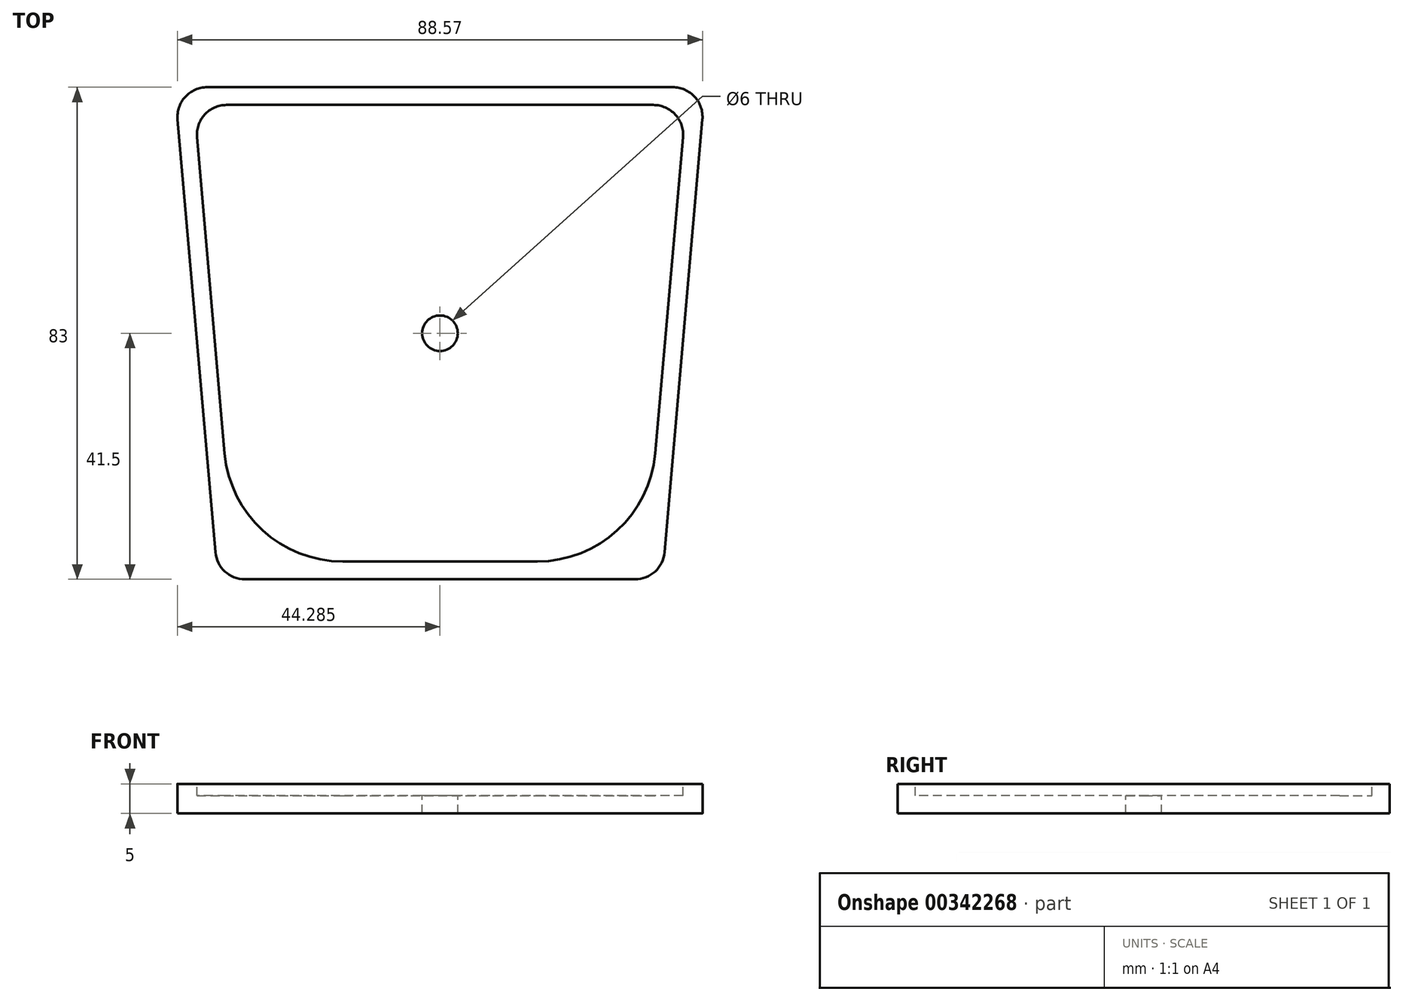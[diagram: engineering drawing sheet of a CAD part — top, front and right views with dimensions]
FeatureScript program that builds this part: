
annotation { "Feature Type Name" : "Feature", "Feature Type Description" : "" }
export const myFeature = defineFeature(function(context is Context, id is Id, definition is map)
    precondition{}
    {
        {
            var Q0;
            Q0=qCreatedBy(makeId("Top.planeOp"),FACE);
            var sketch = newSketch(context, id + "F0", { "sketchPlane" : qUnion([Q0])});
            skLineSegment(sketch, "E0.bottom", {"start": v(-48.45, 0) * mm, "end": v(41.55, 0) * mm});
            skLineSegment(sketch, "E0.top", {"start": v(-40.93, -86) * mm, "end": v(34.02, -86) * mm});
            skLineSegment(sketch, "E0.left", {"start": v(-48.45, 0) * mm, "end": v(-40.93, -86) * mm});
            skLineSegment(sketch, "E0.right", {"start": v(41.55, 0) * mm, "end": v(34.02, -86) * mm});
            skSolve(sketch);
        }
        {
            var Q0;
            Q0=makeQuery(id+"F0.imprint","IMPRINT",FACE,{"disambiguationData":[TD([[makeQuery(id+"F0.imprint","IMPRINT",EDGE,{"derivedFrom":sQuery(id+"F0.wireOp",EDGE,"E0.bottom")}),-1.0]])]});
            extrude(context, id + "F1", {"entities" : qUnion([Q0]), "depth" : 10 * mm});
        }
        {
            var Q0;
            Q0=makeQuery(id+"F1.opExtrude","SWEPT_FACE",FACE,{"disambiguationData":[OSD([sQuery(id+"F0.wireOp",EDGE,"E0.bottom")])]});
            var sketch = newSketch(context, id + "F2", { "sketchPlane" : qUnion([Q0])});
            skLineSegment(sketch, "E1.bottom", {"start": v(-41.55, -40) * mm, "end": v(48.45, -40) * mm});
            skLineSegment(sketch, "E1.top", {"start": v(-41.55, 50) * mm, "end": v(48.45, 50) * mm});
            skLineSegment(sketch, "E1.left", {"start": v(-41.55, -40) * mm, "end": v(-41.55, 50) * mm});
            skLineSegment(sketch, "E1.right", {"start": v(48.45, -40) * mm, "end": v(48.45, 50) * mm});
            skSolve(sketch);
        }
        {
            var Q0;
            {var subQ0=sQuery(id+"F2.wireOp",EDGE,"E1.top");Q0=makeQuery(id+"F2.imprint","IMPRINT",FACE,{"disambiguationData":[TD([[makeQuery(id+"F2.imprint","IMPRINT",EDGE,{"derivedFrom":subQ0}),-1.0]])]});}
            var Q1;
            {var subQ1=sQuery(id+"F0.wireOp",EDGE,"E0.bottom");var subQ2=makeQuery(id+"F1.opExtrude","CAP_EDGE",EDGE,{"disambiguationData":[OSD([subQ1])],"isStart":true});Q1=makeQuery(id+"F2.imprint","IMPRINT",FACE,{"disambiguationData":[TD([[makeQuery(id+"F2.imprint","IMPRINT",EDGE,{"derivedFrom":subQ2}),-1.0]])]});}
            var Q2;
            {var subQ0=sQuery(id+"F2.wireOp",EDGE,"E1.bottom");Q2=makeQuery(id+"F2.imprint","IMPRINT",FACE,{"disambiguationData":[TD([[makeQuery(id+"F2.imprint","IMPRINT",EDGE,{"derivedFrom":subQ0}),1.0]])]});}
            extrude(context, id + "F3", {"entities" : qUnion([Q0, Q1, Q2]), "operationType" : NewBodyOperationType.ADD, "depth" : 10 * mm});
        }
        {
            var Q0;
            Q0=makeQuery(id+"F1.opExtrude","SWEPT_EDGE",EDGE,{"disambiguationData":[OSD([sQuery(id+"F0.wireOp",EDGE,"E0.top"),sQuery(id+"F0.wireOp",EDGE,"E0.left")])]});
            var Q1;
            Q1=makeQuery(id+"F1.opExtrude","SWEPT_EDGE",EDGE,{"disambiguationData":[OSD([sQuery(id+"F0.wireOp",EDGE,"E0.top"),sQuery(id+"F0.wireOp",EDGE,"E0.right")])]});
            fillet(context, id + "F4", {"entities" : qUnion([Q0, Q1]), "radius" : 5 * mm, "tangentPropagation" : true, "allowEdgeOverflow" : false});
        }
        {
            var Q0;
            {var subQ0=sQuery(id+"F2.wireOp",EDGE,"E1.top");var subQ3=sQuery(id+"F2.wireOp",EDGE,"E1.left");var subQ4=sQuery(id+"F2.wireOp",EDGE,"E1.right");Q0=makeQuery(id+"F3.boolean.opBoolean","SPLIT",FACE,{"disambiguationData":[TD([makeQuery(id+"F3.opExtrude","SWEPT_FACE",FACE,{"disambiguationData":[OSD([subQ0])]})])],"derivedFrom":makeQuery(id+"F3.opExtrude","CAP_FACE",FACE,{"disambiguationData":[OSD([sQuery(id+"F2.wireOp",EDGE,"E1.bottom"),subQ0,subQ3,subQ4])],"isStart":true})});}
            var sketch = newSketch(context, id + "F5", { "sketchPlane" : qUnion([Q0])});
            skCircle(sketch, "E2", {"center": v(-28.45, 40) * mm, "radius": 4 * mm});
            skCircle(sketch, "E3", {"center": v(21.55, 40) * mm, "radius": 4 * mm});
            skSolve(sketch);
        }
        {
            var Q0;
            Q0 = qSketchRegion(id + "F5", true);
            extrude(context, id + "F6", {"entities" : qUnion([Q0]), "operationType" : NewBodyOperationType.REMOVE, "oppositeDirection" : true, "depth" : 25 * mm});
        }
        {
            var Q0;
            Q0=makeQuery(id+"F3.opExtrude","SWEPT_EDGE",EDGE,{"disambiguationData":[OSD([sQuery(id+"F2.wireOp",EDGE,"E1.top"),sQuery(id+"F2.wireOp",EDGE,"E1.right")])]});
            var Q1;
            Q1=makeQuery(id+"F3.opExtrude","SWEPT_EDGE",EDGE,{"disambiguationData":[OSD([sQuery(id+"F2.wireOp",EDGE,"E1.top"),sQuery(id+"F2.wireOp",EDGE,"E1.left")])]});
            var Q2;
            Q2=makeQuery(id+"F3.opExtrude","SWEPT_EDGE",EDGE,{"disambiguationData":[OSD([sQuery(id+"F2.wireOp",EDGE,"E1.bottom"),sQuery(id+"F2.wireOp",EDGE,"E1.left")])]});
            var Q3;
            Q3=makeQuery(id+"F3.opExtrude","SWEPT_EDGE",EDGE,{"disambiguationData":[OSD([sQuery(id+"F2.wireOp",EDGE,"E1.bottom"),sQuery(id+"F2.wireOp",EDGE,"E1.right")])]});
            fillet(context, id + "F7", {"entities" : qUnion([Q0, Q1, Q2, Q3]), "radius" : 3 * mm, "tangentPropagation" : true, "allowEdgeOverflow" : false});
        }
        {
            var Q0;
            Q0=makeQuery(id+"F1.opExtrude","CAP_EDGE",EDGE,{"disambiguationData":[OSD([sQuery(id+"F0.wireOp",EDGE,"E0.bottom")])],"isStart":false});
            fillet(context, id + "F8", {"entities" : qUnion([Q0]), "radius" : 3 * mm, "tangentPropagation" : true, "allowEdgeOverflow" : false});
        }
        {
            var Q0;
            Q0=makeQuery(id+"F1.opExtrude","CAP_FACE",FACE,{"disambiguationData":[OSD([sQuery(id+"F0.wireOp",EDGE,"E0.bottom"),sQuery(id+"F0.wireOp",EDGE,"E0.top"),sQuery(id+"F0.wireOp",EDGE,"E0.left"),sQuery(id+"F0.wireOp",EDGE,"E0.right")])],"isStart":false});
            var sketch = newSketch(context, id + "F9", { "sketchPlane" : qUnion([Q0])});
            skLineSegment(sketch, "E4.0", {"start": v(32.55, -6) * mm, "end": v(-39.46, -6) * mm});
            skLineSegment(sketch, "E4.1", {"start": v(37.53, -11.44) * mm, "end": v(32.87, -64.74) * mm});
            skLineSegment(sketch, "E4.2", {"start": v(-19.86, -83) * mm, "end": v(12.95, -83) * mm});
            skLineSegment(sketch, "E4.3", {"start": v(-44.44, -11.44) * mm, "end": v(-39.78, -64.74) * mm});
            skPoint(sketch, "E5.visualSharp", {"position": v(-44.92, -6) * mm});
            skArc(sketch, "E5.filletArc", {"start": v(-39.46, -6) * mm, "mid": v(-43.15, -7.62) * mm, "end": v(-44.44, -11.44) * mm});
            skPoint(sketch, "E6.visualSharp", {"position": v(-38.18, -83) * mm});
            skArc(sketch, "E6.filletArc", {"start": v(-39.78, -64.74) * mm, "mid": v(-33.37, -77.75) * mm, "end": v(-19.86, -83) * mm});
            skPoint(sketch, "E7.visualSharp", {"position": v(31.27, -83) * mm});
            skArc(sketch, "E7.filletArc", {"start": v(12.95, -83) * mm, "mid": v(26.46, -77.75) * mm, "end": v(32.87, -64.74) * mm});
            skPoint(sketch, "E8.visualSharp", {"position": v(38, -6) * mm});
            skArc(sketch, "E8.filletArc", {"start": v(37.53, -11.44) * mm, "mid": v(36.24, -7.62) * mm, "end": v(32.55, -6) * mm});
            skSolve(sketch);
        }
        {
            var Q0;
            Q0=makeQuery(id+"F9.imprint","IMPRINT",FACE,{"disambiguationData":[TD([[makeQuery(id+"F9.imprint","IMPRINT",EDGE,{"derivedFrom":sQuery(id+"F9.wireOp",EDGE,"E4.0")}),1.0]])]});
            extrude(context, id + "F10", {"entities" : qUnion([Q0]), "operationType" : NewBodyOperationType.REMOVE, "oppositeDirection" : true, "depth" : 2 * mm});
        }
        {
            var Q0;
            Q0=makeQuery(id+"F10.boolean.opBoolean","COPY",FACE,{"derivedFrom":makeQuery(id+"F10.opExtrude","CAP_FACE",FACE,{"disambiguationData":[OSD([sQuery(id+"F9.wireOp",EDGE,"E4.0"),sQuery(id+"F9.wireOp",EDGE,"E4.1"),sQuery(id+"F9.wireOp",EDGE,"E4.2"),sQuery(id+"F9.wireOp",EDGE,"E4.3"),sQuery(id+"F9.wireOp",EDGE,"E5.filletArc"),sQuery(id+"F9.wireOp",EDGE,"E6.filletArc"),sQuery(id+"F9.wireOp",EDGE,"E7.filletArc"),sQuery(id+"F9.wireOp",EDGE,"E8.filletArc")])],"isStart":false})});
            var sketch = newSketch(context, id + "F11", { "sketchPlane" : qUnion([Q0])});
            skLineSegment(sketch, "E9", {"start": v(-3.45, -6) * mm, "end": v(-3.45, -83) * mm, "construction": true});
            skCircle(sketch, "E10", {"center": v(-3.45, -44.5) * mm, "radius": 3 * mm});
            skSolve(sketch);
        }
        {
            var Q0;
            Q0 = qSketchRegion(id + "F11", true);
            extrude(context, id + "F12", {"entities" : qUnion([Q0]), "operationType" : NewBodyOperationType.REMOVE, "oppositeDirection" : true, "depth" : 25 * mm});
        }
        {
            var Q0;
            Q0=makeQuery(id+"F3.opExtrude","SWEPT_FACE",FACE,{"disambiguationData":[OSD([sQuery(id+"F2.wireOp",EDGE,"E1.right")])]});
            var sketch = newSketch(context, id + "F13", { "sketchPlane" : qUnion([Q0])});
            skLineSegment(sketch, "E11.bottom", {"start": v(3, 62.62) * mm, "end": v(-30.66, 62.62) * mm});
            skLineSegment(sketch, "E11.top", {"start": v(3, -58) * mm, "end": v(-30.66, -58) * mm});
            skLineSegment(sketch, "E11.left", {"start": v(3, 62.62) * mm, "end": v(3, -58) * mm});
            skLineSegment(sketch, "E11.right", {"start": v(-30.66, 62.62) * mm, "end": v(-30.66, -58) * mm});
            skSolve(sketch);
        }
        {
            var Q0;
            Q0 = qSketchRegion(id + "F13", true);
            extrude(context, id + "F14", {"entities" : qUnion([Q0]), "operationType" : NewBodyOperationType.REMOVE, "endBound" : BoundingType.THROUGH_ALL, "oppositeDirection" : true, "depth" : 25 * mm});
        }
        {
            var Q0;
            Q0=makeQuery(id+"F14.boolean.opBoolean","INTERSECT",EDGE,{"derivedFrom":[makeQuery(id+"F1.opExtrude","SWEPT_FACE",FACE,{"disambiguationData":[OSD([sQuery(id+"F0.wireOp",EDGE,"E0.left")])]}),makeQuery(id+"F14.opExtrude","SWEPT_FACE",FACE,{"disambiguationData":[OSD([sQuery(id+"F13.wireOp",EDGE,"E11.left")])]})]});
            var Q1;
            Q1=makeQuery(id+"F14.boolean.opBoolean","INTERSECT",EDGE,{"derivedFrom":[makeQuery(id+"F1.opExtrude","SWEPT_FACE",FACE,{"disambiguationData":[OSD([sQuery(id+"F0.wireOp",EDGE,"E0.right")])]}),makeQuery(id+"F14.opExtrude","SWEPT_FACE",FACE,{"disambiguationData":[OSD([sQuery(id+"F13.wireOp",EDGE,"E11.left")])]})]});
            fillet(context, id + "F15", {"entities" : qUnion([Q0, Q1]), "radius" : 5 * mm, "tangentPropagation" : true, "allowEdgeOverflow" : false});
        }
        {
            var Q0;
            Q0=qCreatedBy(makeId("Right.planeOp"),FACE);
            var sketch = newSketch(context, id + "F16", { "sketchPlane" : qUnion([Q0])});
            skLineSegment(sketch, "E12.bottom", {"start": v(-0.38, 5) * mm, "end": v(-90.61, 5) * mm});
            skLineSegment(sketch, "E12.top", {"start": v(-0.38, -7.92) * mm, "end": v(-90.61, -7.92) * mm});
            skLineSegment(sketch, "E12.left", {"start": v(-0.38, 5) * mm, "end": v(-0.38, -7.92) * mm});
            skLineSegment(sketch, "E12.right", {"start": v(-90.61, 5) * mm, "end": v(-90.61, -7.92) * mm});
            skSolve(sketch);
        }
        {
            var Q0;
            Q0 = qSketchRegion(id + "F16", true);
            extrude(context, id + "F17", {"entities" : qUnion([Q0]), "operationType" : NewBodyOperationType.REMOVE, "endBound" : BoundingType.SYMMETRIC, "oppositeDirection" : true, "depth" : 100 * mm});
        }
    });
